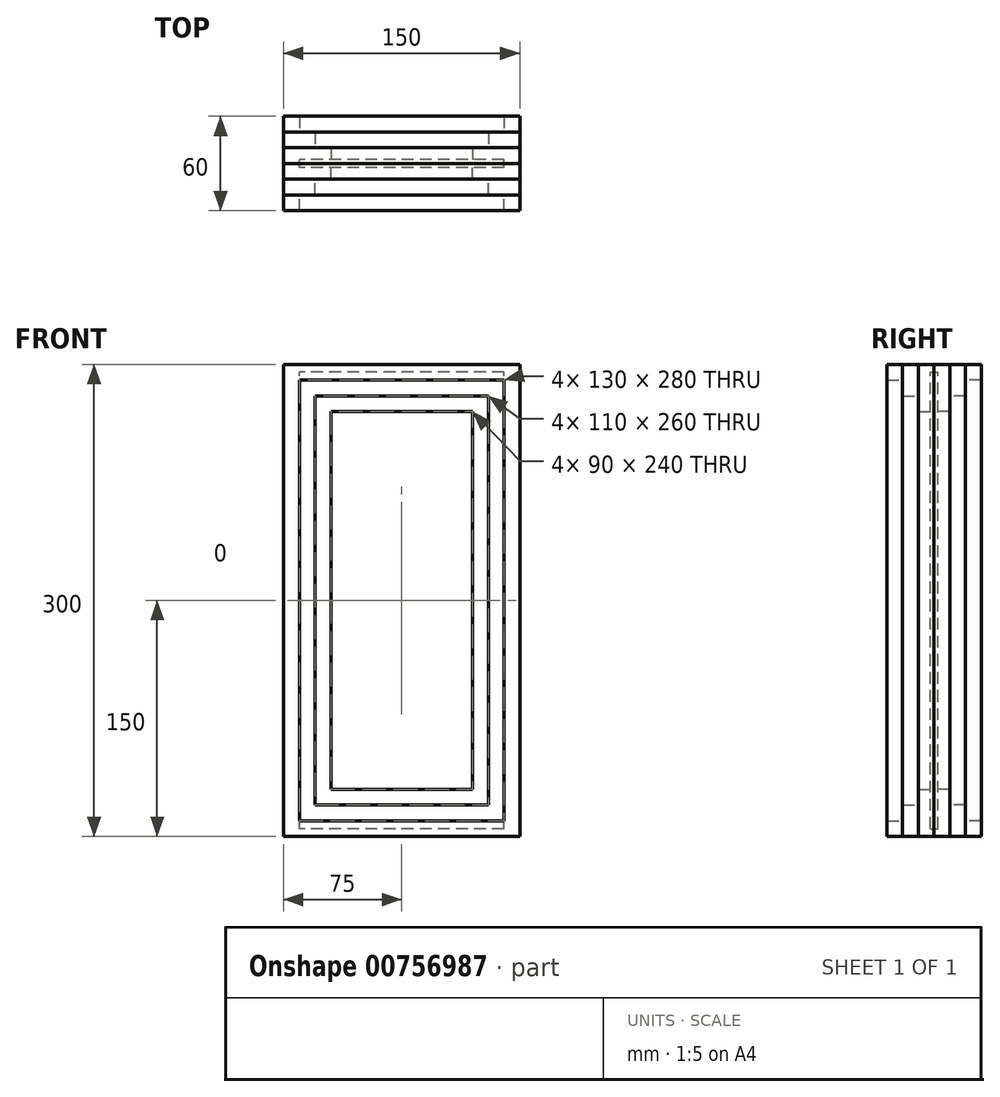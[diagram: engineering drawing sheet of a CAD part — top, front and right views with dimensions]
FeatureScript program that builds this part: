
annotation { "Feature Type Name" : "Feature", "Feature Type Description" : "" }
export const myFeature = defineFeature(function(context is Context, id is Id, definition is map)
    precondition{}
    {
        {
            var Q0;
            Q0=qCreatedBy(makeId("Front.planeOp"),FACE);
            var sketch = newSketch(context, id + "F0", { "sketchPlane" : qUnion([Q0])});
            skLineSegment(sketch, "E0.bottom", {"start": v(75, -150) * mm, "end": v(-75, -150) * mm});
            skLineSegment(sketch, "E0.top", {"start": v(75, 150) * mm, "end": v(-75, 150) * mm});
            skLineSegment(sketch, "E0.left", {"start": v(75, -150) * mm, "end": v(75, 150) * mm});
            skLineSegment(sketch, "E0.right", {"start": v(-75, -150) * mm, "end": v(-75, 150) * mm});
            skPoint(sketch, "E0.middle", {"position": v(0, 0) * mm});
            skLineSegment(sketch, "E1.bottom", {"start": v(45, -120) * mm, "end": v(-45, -120) * mm});
            skLineSegment(sketch, "E1.top", {"start": v(45, 120) * mm, "end": v(-45, 120) * mm});
            skLineSegment(sketch, "E1.left", {"start": v(45, -120) * mm, "end": v(45, 120) * mm});
            skLineSegment(sketch, "E1.right", {"start": v(-45, -120) * mm, "end": v(-45, 120) * mm});
            skSolve(sketch);
        }
        {
            var Q0;
            Q0 = qSketchRegion(id + "F0", true);
            extrude(context, id + "F1", {"entities" : qUnion([Q0]), "depth" : 10 * mm, "offsetDistance" : 25 * mm});
        }
        {
            var Q0;
            Q0=makeQuery(id+"F1.opExtrude","CAP_FACE",FACE,{"disambiguationData":[OSD([sQuery(id+"F0.wireOp",EDGE,"E0.bottom"),sQuery(id+"F0.wireOp",EDGE,"E0.top"),sQuery(id+"F0.wireOp",EDGE,"E0.left"),sQuery(id+"F0.wireOp",EDGE,"E0.right"),sQuery(id+"F0.wireOp",EDGE,"E1.bottom"),sQuery(id+"F0.wireOp",EDGE,"E1.top"),sQuery(id+"F0.wireOp",EDGE,"E1.left"),sQuery(id+"F0.wireOp",EDGE,"E1.right")])],"isStart":false});
            var sketch = newSketch(context, id + "F2", { "sketchPlane" : qUnion([Q0])});
            skLineSegment(sketch, "E2.0", {"start": v(75, 150) * mm, "end": v(-75, 150) * mm});
            skLineSegment(sketch, "E3.0", {"start": v(-75, -150) * mm, "end": v(-75, 150) * mm});
            skLineSegment(sketch, "E4.0", {"start": v(75, -150) * mm, "end": v(75, 150) * mm});
            skLineSegment(sketch, "E5.0", {"start": v(75, -150) * mm, "end": v(-75, -150) * mm});
            skLineSegment(sketch, "E6.bottom", {"start": v(55, -130) * mm, "end": v(-55, -130) * mm});
            skLineSegment(sketch, "E6.top", {"start": v(55, 130) * mm, "end": v(-55, 130) * mm});
            skLineSegment(sketch, "E6.left", {"start": v(55, -130) * mm, "end": v(55, 130) * mm});
            skLineSegment(sketch, "E6.right", {"start": v(-55, -130) * mm, "end": v(-55, 130) * mm});
            skPoint(sketch, "E6.middle", {"position": v(0, 0) * mm});
            skSolve(sketch);
        }
        {
            var Q0;
            Q0 = qSketchRegion(id + "F2", true);
            extrude(context, id + "F3", {"entities" : qUnion([Q0]), "depth" : 10 * mm, "offsetDistance" : 25 * mm});
        }
        {
            var Q0;
            Q0=makeQuery(id+"F3.opExtrude","CAP_FACE",FACE,{"disambiguationData":[OSD([sQuery(id+"F2.wireOp",EDGE,"E2.0"),sQuery(id+"F2.wireOp",EDGE,"E3.0"),sQuery(id+"F2.wireOp",EDGE,"E4.0"),sQuery(id+"F2.wireOp",EDGE,"E5.0"),sQuery(id+"F2.wireOp",EDGE,"E6.bottom"),sQuery(id+"F2.wireOp",EDGE,"E6.top"),sQuery(id+"F2.wireOp",EDGE,"E6.left"),sQuery(id+"F2.wireOp",EDGE,"E6.right")])],"isStart":false});
            var sketch = newSketch(context, id + "F4", { "sketchPlane" : qUnion([Q0])});
            skLineSegment(sketch, "E7.0", {"start": v(75, 150) * mm, "end": v(-75, 150) * mm});
            skLineSegment(sketch, "E8.0", {"start": v(-75, -150) * mm, "end": v(-75, 150) * mm});
            skLineSegment(sketch, "E9.0", {"start": v(75, -150) * mm, "end": v(75, 150) * mm});
            skLineSegment(sketch, "E10.0", {"start": v(75, -150) * mm, "end": v(-75, -150) * mm});
            skLineSegment(sketch, "E11.bottom", {"start": v(65, -140) * mm, "end": v(-65, -140) * mm});
            skLineSegment(sketch, "E11.top", {"start": v(65, 140) * mm, "end": v(-65, 140) * mm});
            skLineSegment(sketch, "E11.left", {"start": v(65, -140) * mm, "end": v(65, 140) * mm});
            skLineSegment(sketch, "E11.right", {"start": v(-65, -140) * mm, "end": v(-65, 140) * mm});
            skPoint(sketch, "E11.middle", {"position": v(0, 0) * mm});
            skSolve(sketch);
        }
        {
            var Q0;
            Q0 = qSketchRegion(id + "F4", true);
            extrude(context, id + "F5", {"entities" : qUnion([Q0]), "depth" : 10 * mm, "offsetDistance" : 25 * mm});
        }
        {
            var Q0;
            Q0=makeQuery(id+"F1.opExtrude","SWEPT_BODY",BODY,{"disambiguationData":[OSD([sQuery(id+"F0.wireOp",EDGE,"E0.bottom"),sQuery(id+"F0.wireOp",EDGE,"E0.top"),sQuery(id+"F0.wireOp",EDGE,"E0.left"),sQuery(id+"F0.wireOp",EDGE,"E0.right"),sQuery(id+"F0.wireOp",EDGE,"E1.bottom"),sQuery(id+"F0.wireOp",EDGE,"E1.top"),sQuery(id+"F0.wireOp",EDGE,"E1.left"),sQuery(id+"F0.wireOp",EDGE,"E1.right")])]});
            var Q1;
            Q1=makeQuery(id+"F3.opExtrude","SWEPT_BODY",BODY,{"disambiguationData":[OSD([sQuery(id+"F2.wireOp",EDGE,"E2.0"),sQuery(id+"F2.wireOp",EDGE,"E3.0"),sQuery(id+"F2.wireOp",EDGE,"E4.0"),sQuery(id+"F2.wireOp",EDGE,"E5.0"),sQuery(id+"F2.wireOp",EDGE,"E6.bottom"),sQuery(id+"F2.wireOp",EDGE,"E6.top"),sQuery(id+"F2.wireOp",EDGE,"E6.left"),sQuery(id+"F2.wireOp",EDGE,"E6.right")])]});
            var Q2;
            Q2=makeQuery(id+"F5.opExtrude","SWEPT_BODY",BODY,{"disambiguationData":[OSD([sQuery(id+"F4.wireOp",EDGE,"E7.0"),sQuery(id+"F4.wireOp",EDGE,"E8.0"),sQuery(id+"F4.wireOp",EDGE,"E9.0"),sQuery(id+"F4.wireOp",EDGE,"E10.0"),sQuery(id+"F4.wireOp",EDGE,"E11.bottom"),sQuery(id+"F4.wireOp",EDGE,"E11.top"),sQuery(id+"F4.wireOp",EDGE,"E11.left"),sQuery(id+"F4.wireOp",EDGE,"E11.right")])]});
            var Q3;
            Q3=qCreatedBy(makeId("Front.planeOp"),FACE);
            mirror(context, id + "F6", {"entities" : qUnion([Q0, Q1, Q2]), "mirrorPlane" : qUnion([Q3])});
        }
        {
            var Q0;
            Q0=qCreatedBy(makeId("Front.planeOp"),FACE);
            var sketch = newSketch(context, id + "F7", { "sketchPlane" : qUnion([Q0])});
            skLineSegment(sketch, "E12.bottom", {"start": v(65, -145) * mm, "end": v(-65, -145) * mm});
            skLineSegment(sketch, "E12.top", {"start": v(65, 145) * mm, "end": v(-65, 145) * mm});
            skLineSegment(sketch, "E12.left", {"start": v(65, -145) * mm, "end": v(65, 145) * mm});
            skLineSegment(sketch, "E12.right", {"start": v(-65, -145) * mm, "end": v(-65, 145) * mm});
            skPoint(sketch, "E12.middle", {"position": v(0, 0) * mm});
            skSolve(sketch);
        }
        {
            var Q0;
            Q0 = qSketchRegion(id + "F7", true);
            extrude(context, id + "F8", {"entities" : qUnion([Q0]), "endBound" : BoundingType.SYMMETRIC, "depth" : 5 * mm, "offsetDistance" : 25 * mm});
        }
    });
